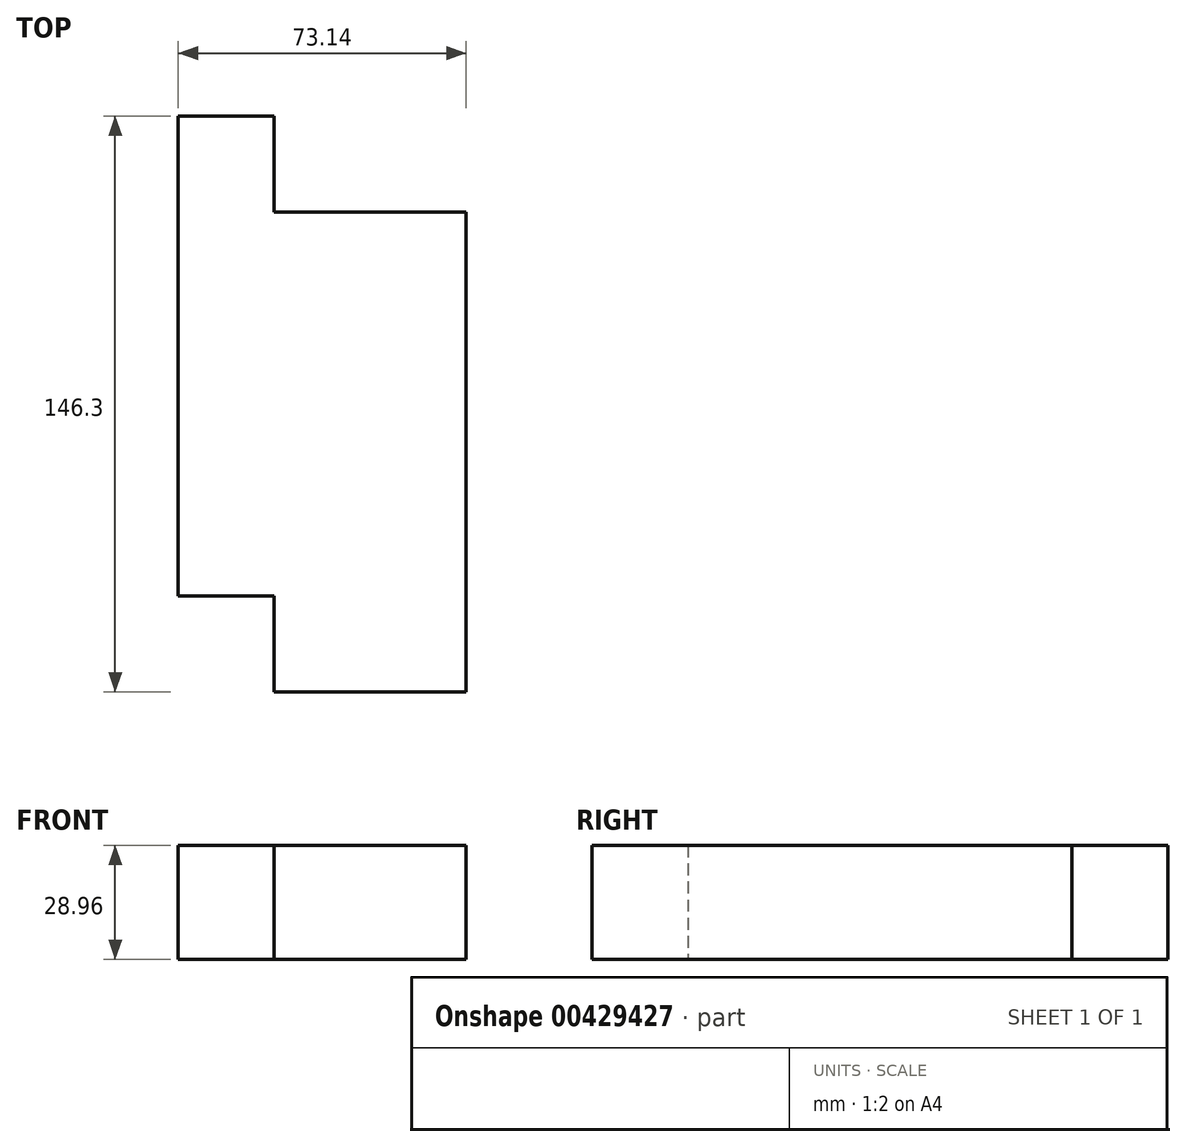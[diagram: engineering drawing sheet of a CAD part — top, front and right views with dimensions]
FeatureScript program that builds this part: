
annotation { "Feature Type Name" : "Feature", "Feature Type Description" : "" }
export const myFeature = defineFeature(function(context is Context, id is Id, definition is map)
    precondition{}
    {
        {
            var Q0;
            Q0=qCreatedBy(makeId("Top.planeOp"),FACE);
            var sketch = newSketch(context, id + "F0", { "sketchPlane" : qUnion([Q0])});
            skLineSegment(sketch, "E0.bottom", {"start": v(-77.66, 89.54) * mm, "end": v(-53.28, 89.54) * mm});
            skLineSegment(sketch, "E0.top", {"start": v(-77.66, -32.38) * mm, "end": v(-53.28, -32.38) * mm});
            skLineSegment(sketch, "E0.left", {"start": v(-77.66, 89.54) * mm, "end": v(-77.66, -32.38) * mm});
            skLineSegment(sketch, "E0.right", {"start": v(-53.28, 89.54) * mm, "end": v(-53.28, -32.38) * mm});
            skLineSegment(sketch, "E1.bottom", {"start": v(-53.28, 65.16) * mm, "end": v(-28.9, 65.16) * mm});
            skLineSegment(sketch, "E1.top", {"start": v(-53.28, -56.76) * mm, "end": v(-28.9, -56.76) * mm});
            skLineSegment(sketch, "E1.left", {"start": v(-53.28, 65.16) * mm, "end": v(-53.28, -56.76) * mm});
            skLineSegment(sketch, "E1.right", {"start": v(-28.9, 65.16) * mm, "end": v(-28.9, -56.76) * mm});
            skLineSegment(sketch, "E2.bottom", {"start": v(-28.9, 65.16) * mm, "end": v(-4.52, 65.16) * mm});
            skLineSegment(sketch, "E2.top", {"start": v(-28.9, -56.76) * mm, "end": v(-4.52, -56.76) * mm});
            skLineSegment(sketch, "E2.right", {"start": v(-4.52, 65.16) * mm, "end": v(-4.52, -56.76) * mm});
            skSolve(sketch);
        }
        {
            var Q0;
            Q0 = qSketchRegion(id + "F0", true);
            extrude(context, id + "F1", {"entities" : qUnion([Q0]), "depth" : 28.96 * mm});
        }
    });
